# Revit family: Albardilla MAP remate.C-1
name_source: partatom
category: Modelos genéricos
units: mm (PartAtom-declared; Revit-internal decimal feet)

## family parameters
Compartido = No
Corte con vacíos al cargar = No
Cota de conector redondo = Diámetro de uso
Puede alojar armadura = No
Punto de cálculo de habitación = No
Se basa en plano de trabajo = No
Siempre vertical = No
Tipo de pieza = Normal

## types (7) — shared parameters
Descripción = Pieza de hormigón polímero con anclaje de acero inoxidable.
Fabricante = ULMA Architectural Solutions
Material = Hormigón polímero STONEO. Color C-1
URL = https://www.ulmaarchitectural.com
zero-valued in all types: Elevación por defecto

## per-type parameters (varying)
| type | Altura | Ancho | Ancho doble | Ancho total | Ancho vaciado | Longitud vaciado | Mitad | Modelo | Visibilidad dos filas | Visibilidad una fila |
| RMAP12 | 44 mm  [stored 0.144357 ft] | 120 mm  [stored 0.393701 ft] | 30 mm  [stored 0.0984252 ft] | 170 mm  [stored 0.557743 ft] | 140 mm  [stored 0.459318 ft] | 735 mm | 85 mm  [stored 0.278871 ft] | Albardilla MAP12 remate | No | Sí |
| RMAP14 | 44 mm  [stored 0.144357 ft] | 140 mm  [stored 0.459318 ft] | 35 mm  [stored 0.114829 ft] | 190 mm  [stored 0.62336 ft] | 160 mm | 735 mm | 95 mm | Albardilla MAP14 remate | No | Sí |
| RMAP17 | 44 mm  [stored 0.144357 ft] | 170 mm  [stored 0.557743 ft] | 43 mm | 220 mm  [stored 0.721785 ft] | 190 mm  [stored 0.62336 ft] | 735 mm | 110 mm  [stored 0.360892 ft] | Albardilla MAP17 remate | No | Sí |
| RMAP22 | 44 mm  [stored 0.144357 ft] | 220 mm  [stored 0.721785 ft] | 55 mm  [stored 0.180446 ft] | 270 mm  [stored 0.885827 ft] | 240 mm  [stored 0.787402 ft] | 735 mm | 135 mm  [stored 0.442913 ft] | Albardilla MAP22 remate | No | Sí |
| RMAP25 | 46 mm  [stored 0.150919 ft] | 260 mm  [stored 0.853018 ft] | 65 mm  [stored 0.213255 ft] | 310 mm  [stored 1.01706 ft] | 280 mm  [stored 0.918635 ft] | 485 mm  [stored 1.59121 ft] | 155 mm  [stored 0.50853 ft] | Albardilla MAP25 remate | No | Sí |
| RMAP30 | 46 mm  [stored 0.150919 ft] | 310 mm  [stored 1.01706 ft] | 78 mm | 360 mm  [stored 1.1811 ft] | 330 mm  [stored 1.08268 ft] | 485 mm  [stored 1.59121 ft] | 180 mm  [stored 0.590551 ft] | Albardilla MAP30 remate | Sí | No |
| RMAP19 | 44 mm  [stored 0.144357 ft] | 190 mm  [stored 0.62336 ft] | 48 mm | 240 mm  [stored 0.787402 ft] | 210 mm | 735 mm | 120 mm  [stored 0.393701 ft] | Albardilla MAP19 remate | No | Sí |

note: column(s) folded — value = type name in every type: Código de montaje

note: [stored X ft] marks values corroborated as IEEE doubles in the binary element streams (Revit-internal decimal feet)
